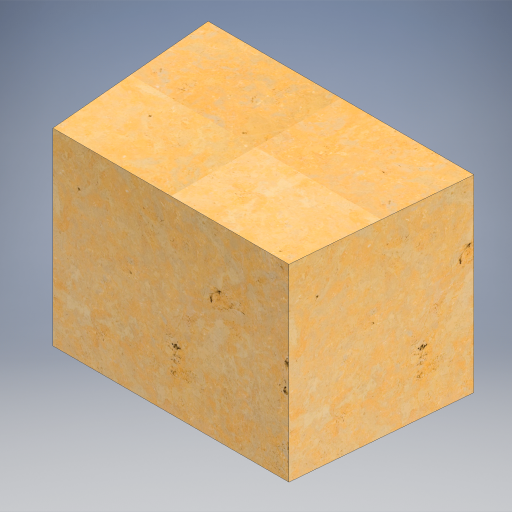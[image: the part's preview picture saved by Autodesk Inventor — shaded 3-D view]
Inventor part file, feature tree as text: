
AUTODESK INVENTOR PART (.ipt)
format: ipt  version: 2023 (Build 270158030, 158C)  size: 543,744 bytes
history: native  units: in
note: dims shown in document units (in); Inventor stores cm internally (conversion verified against a paired STEP export)
features: extrude x1, sketch x1
ambient origin geometry x8: Origin, YZ Plane, XZ Plane, XY Plane, X Axis, Y Axis, Z Axis, Center Point
bodies: Solid1 (feature_tree)
feature tree (2):
  extrude  "Extrusion1"  Depth=24.0in
  sketch  "Sketch1"  dims[d0=33.8125in d1=24.0in d2=0.0687in d3=24.0in d4=0.0in]
